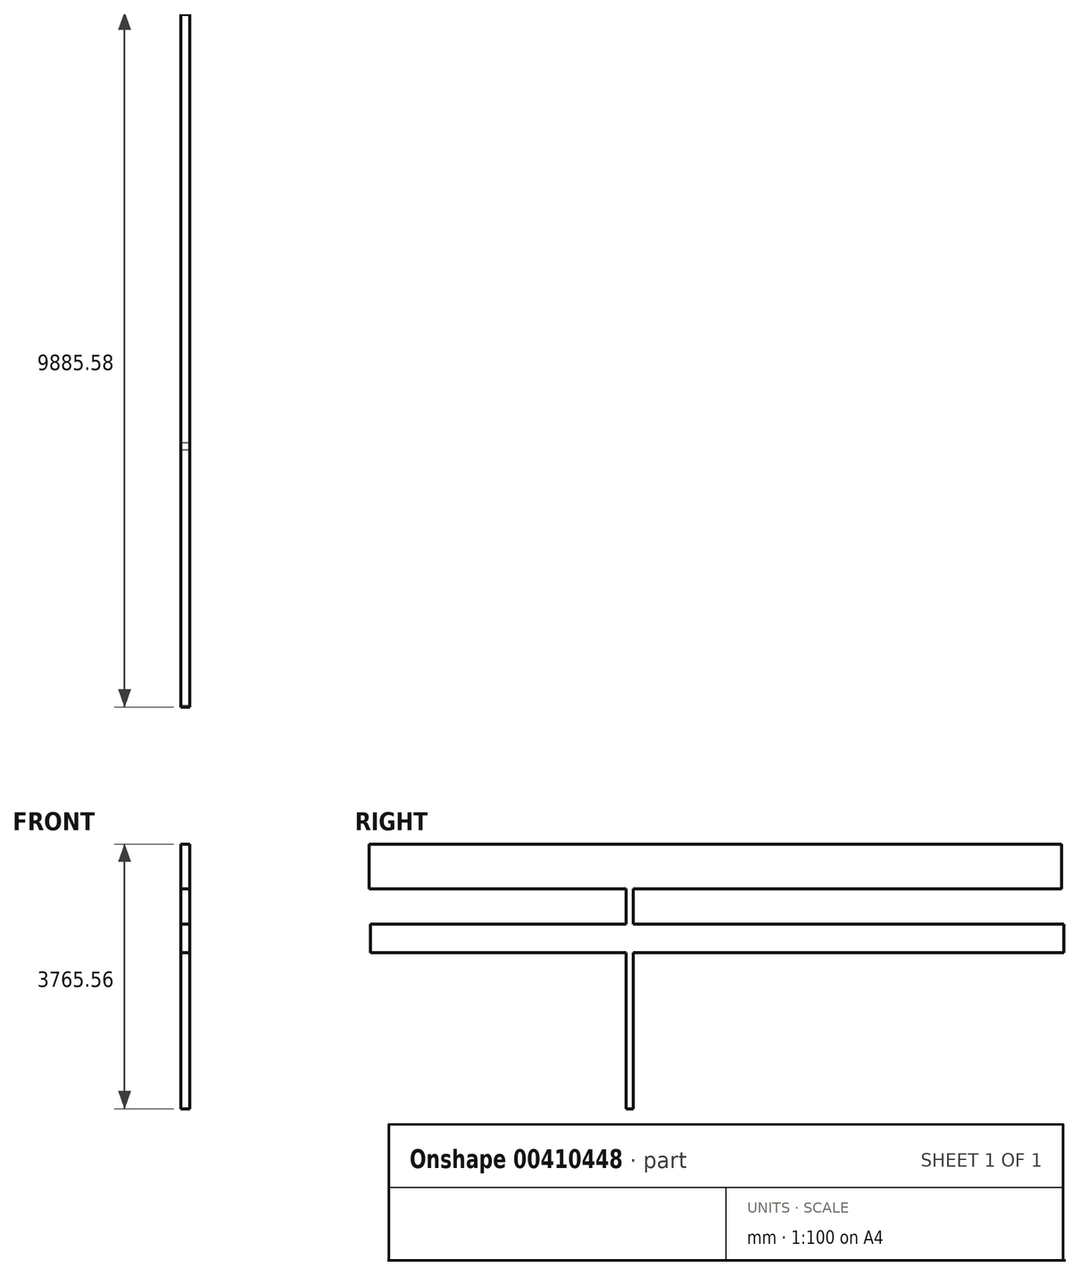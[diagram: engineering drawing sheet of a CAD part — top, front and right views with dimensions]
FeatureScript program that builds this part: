
annotation { "Feature Type Name" : "Feature", "Feature Type Description" : "" }
export const myFeature = defineFeature(function(context is Context, id is Id, definition is map)
    precondition{}
    {
        {
            var Q0;
            Q0=qCreatedBy(makeId("Right.planeOp"),FACE);
            var sketch = newSketch(context, id + "F0", { "sketchPlane" : qUnion([Q0])});
            skLineSegment(sketch, "E0.bottom", {"start": v(50.8, 1882.78) * mm, "end": v(-50.8, 1882.78) * mm});
            skLineSegment(sketch, "E0.top", {"start": v(50.8, -1882.78) * mm, "end": v(-50.8, -1882.78) * mm});
            skLineSegment(sketch, "E0.left", {"start": v(50.8, 1882.78) * mm, "end": v(50.8, -1882.78) * mm});
            skLineSegment(sketch, "E0.right", {"start": v(-50.8, 1882.78) * mm, "end": v(-50.8, -1882.78) * mm});
            skPoint(sketch, "E0.middle", {"position": v(0, 0) * mm});
            skLineSegment(sketch, "E1.bottom", {"start": v(-50.8, 1882.78) * mm, "end": v(6146.8, 1882.78) * mm});
            skLineSegment(sketch, "E1.top", {"start": v(-50.8, 1247.78) * mm, "end": v(6146.8, 1247.78) * mm});
            skLineSegment(sketch, "E1.left", {"start": v(-50.8, 1882.78) * mm, "end": v(-50.8, 1247.78) * mm});
            skLineSegment(sketch, "E1.right", {"start": v(6146.8, 1882.78) * mm, "end": v(6146.8, 1247.77) * mm});
            skLineSegment(sketch, "E2.bottom", {"start": v(-50.8, 1882.78) * mm, "end": v(-3708.4, 1882.78) * mm});
            skLineSegment(sketch, "E2.top", {"start": v(-50.8, 1247.78) * mm, "end": v(-3708.4, 1247.77) * mm});
            skLineSegment(sketch, "E2.right", {"start": v(-3708.4, 1882.77) * mm, "end": v(-3708.4, 1247.77) * mm});
            skLineSegment(sketch, "E3.bottom", {"start": v(-3694.5, 339.72) * mm, "end": v(6177.18, 339.72) * mm});
            skLineSegment(sketch, "E3.top", {"start": v(-3694.5, 746.13) * mm, "end": v(6177.18, 746.13) * mm});
            skLineSegment(sketch, "E3.left", {"start": v(-3694.5, 339.72) * mm, "end": v(-3694.5, 746.13) * mm});
            skLineSegment(sketch, "E3.right", {"start": v(6177.18, 339.72) * mm, "end": v(6177.18, 746.13) * mm});
            skSolve(sketch);
        }
        {
            var Q0;
            Q0 = qSketchRegion(id + "F0", true);
            extrude(context, id + "F1", {"entities" : qUnion([Q0]), "depth" : 127 * mm, "offsetDistance" : 25.4 * mm});
        }
    });
